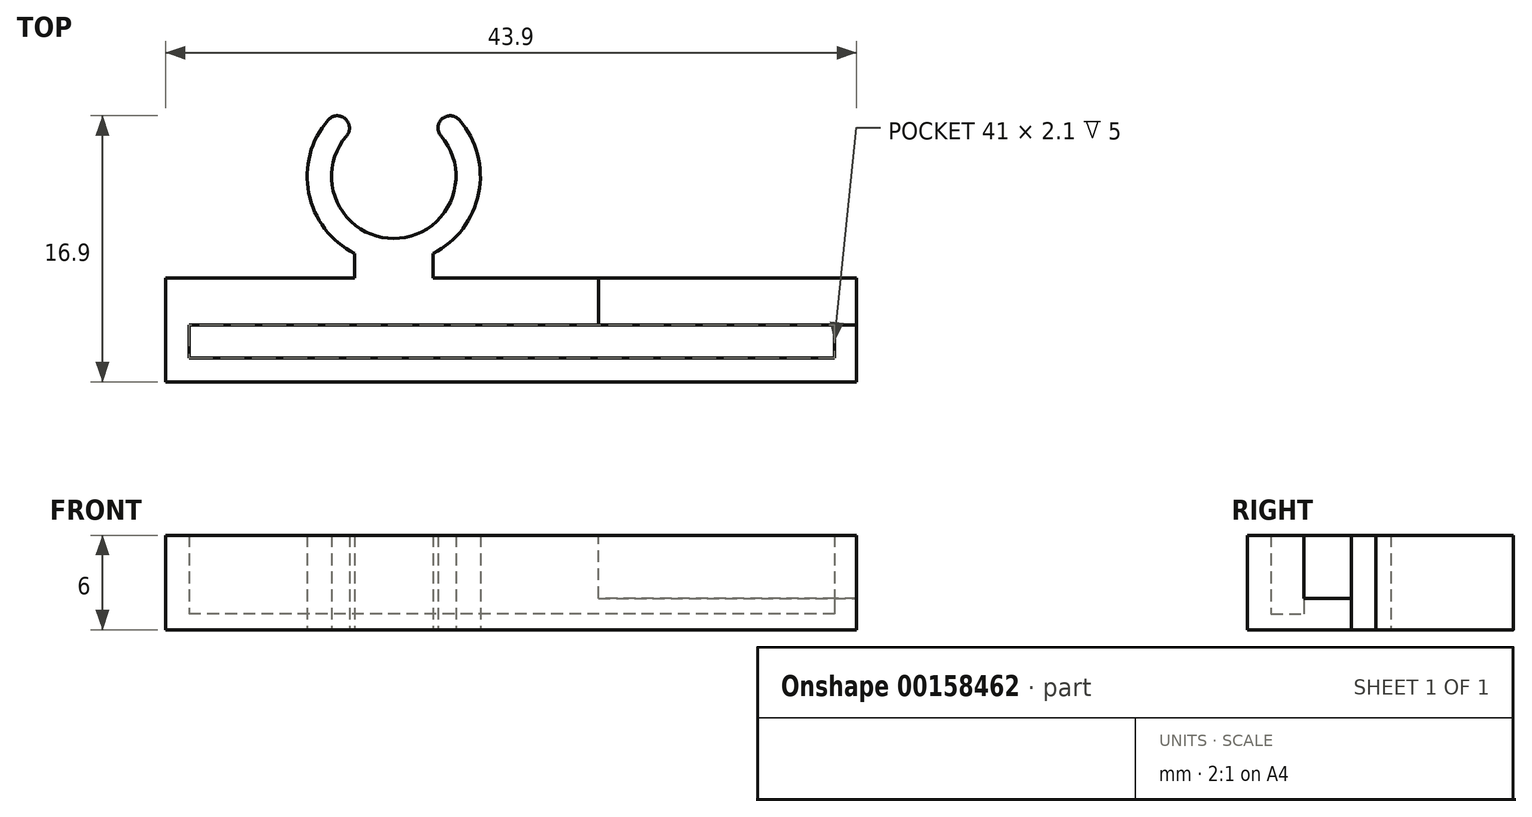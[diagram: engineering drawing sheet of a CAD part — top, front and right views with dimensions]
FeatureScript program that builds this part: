
annotation { "Feature Type Name" : "Feature", "Feature Type Description" : "" }
export const myFeature = defineFeature(function(context is Context, id is Id, definition is map)
    precondition{}
    {
        {
            var Q0;
            Q0=qCreatedBy(makeId("Top.planeOp"),FACE);
            var sketch = newSketch(context, id + "F0", { "sketchPlane" : qUnion([Q0])});
            skArc(sketch, "E0", {"start": v(-3, 2.57) * mm, "mid": v(0, -3.95) * mm, "end": v(3, 2.57) * mm});
            skArc(sketch, "E1", {"start": v(-4.18, 3.58) * mm, "mid": v(-5.4, -1.07) * mm, "end": v(-2.5, -4.9) * mm});
            skLineSegment(sketch, "E2", {"start": v(-3, 2.57) * mm, "end": v(3, 2.57) * mm, "construction": true});
            skLineSegment(sketch, "E3", {"start": v(-3, 2.57) * mm, "end": v(0, 0) * mm, "construction": true});
            skArc(sketch, "E4", {"start": v(-3, 2.57) * mm, "mid": v(-3.08, 3.66) * mm, "end": v(-4.18, 3.58) * mm});
            skLineSegment(sketch, "E5", {"start": v(0, 0) * mm, "end": v(0, 2.57) * mm, "construction": true});
            skArc(sketch, "E6.MirrorCS", {"start": v(3, 2.57) * mm, "mid": v(3.08, 3.66) * mm, "end": v(4.18, 3.58) * mm});
            skLineSegment(sketch, "E7.bottom", {"start": v(-14.5, -6.45) * mm, "end": v(-2.5, -6.45) * mm});
            skLineSegment(sketch, "E7.top", {"start": v(-14.5, -13.05) * mm, "end": v(29.4, -13.05) * mm});
            skLineSegment(sketch, "E7.left", {"start": v(-14.5, -6.45) * mm, "end": v(-14.5, -13.05) * mm});
            skLineSegment(sketch, "E7.right", {"start": v(29.4, -6.45) * mm, "end": v(29.4, -13.05) * mm});
            skLineSegment(sketch, "E8", {"start": v(-2.5, -4.9) * mm, "end": v(-2.5, -6.45) * mm});
            skLineSegment(sketch, "E9", {"start": v(2.5, -4.9) * mm, "end": v(2.5, -6.45) * mm});
            skLineSegment(sketch, "E10.bottom", {"start": v(-13, -9.45) * mm, "end": v(28, -9.45) * mm});
            skLineSegment(sketch, "E10.top", {"start": v(-13, -11.55) * mm, "end": v(28, -11.55) * mm});
            skLineSegment(sketch, "E10.left", {"start": v(-13, -9.45) * mm, "end": v(-13, -11.55) * mm});
            skLineSegment(sketch, "E10.right", {"start": v(28, -9.45) * mm, "end": v(28, -11.55) * mm});
            skLineSegment(sketch, "E11.trimOffspring", {"start": v(2.5, -6.45) * mm, "end": v(29.4, -6.45) * mm});
            skArc(sketch, "E12.trimOffspring", {"start": v(2.5, -4.9) * mm, "mid": v(5.4, -1.07) * mm, "end": v(4.18, 3.58) * mm});
            skSolve(sketch);
        }
        {
            var Q0;
            Q0 = qSketchRegion(id + "F0", true);
            extrude(context, id + "F1", {"entities" : qUnion([Q0]), "depth" : 6 * mm});
        }
        {
            var Q0;
            Q0=makeQuery(id+"F1.opExtrude","CAP_FACE",FACE,{"disambiguationData":[OSD([sQuery(id+"F0.wireOp",EDGE,"E0"),sQuery(id+"F0.wireOp",EDGE,"E1"),sQuery(id+"F0.wireOp",EDGE,"E4"),sQuery(id+"F0.wireOp",EDGE,"E6.MirrorCS"),sQuery(id+"F0.wireOp",EDGE,"E7.bottom"),sQuery(id+"F0.wireOp",EDGE,"E7.top"),sQuery(id+"F0.wireOp",EDGE,"E7.left"),sQuery(id+"F0.wireOp",EDGE,"E7.right"),sQuery(id+"F0.wireOp",EDGE,"E8"),sQuery(id+"F0.wireOp",EDGE,"E9"),sQuery(id+"F0.wireOp",EDGE,"E10.bottom"),sQuery(id+"F0.wireOp",EDGE,"E10.top"),sQuery(id+"F0.wireOp",EDGE,"E10.left"),sQuery(id+"F0.wireOp",EDGE,"E10.right"),sQuery(id+"F0.wireOp",EDGE,"E11.trimOffspring"),sQuery(id+"F0.wireOp",EDGE,"E12.trimOffspring")])],"isStart":false});
            var sketch = newSketch(context, id + "F2", { "sketchPlane" : qUnion([Q0])});
            skLineSegment(sketch, "E13.bottom", {"start": v(29.4, -6.45) * mm, "end": v(13, -6.45) * mm});
            skLineSegment(sketch, "E13.top", {"start": v(29.4, -9.45) * mm, "end": v(13, -9.45) * mm});
            skLineSegment(sketch, "E13.left", {"start": v(29.4, -6.45) * mm, "end": v(29.4, -9.45) * mm});
            skLineSegment(sketch, "E13.right", {"start": v(13, -6.45) * mm, "end": v(13, -9.45) * mm});
            skSolve(sketch);
        }
        {
            var Q0;
            Q0 = qSketchRegion(id + "F2", true);
            extrude(context, id + "F3", {"entities" : qUnion([Q0]), "operationType" : NewBodyOperationType.REMOVE, "oppositeDirection" : true, "depth" : 4 * mm});
        }
        {
            var Q0;
            Q0=makeQuery(id+"F1.opExtrude","CAP_FACE",FACE,{"disambiguationData":[OSD([sQuery(id+"F0.wireOp",EDGE,"E0"),sQuery(id+"F0.wireOp",EDGE,"E1"),sQuery(id+"F0.wireOp",EDGE,"E4"),sQuery(id+"F0.wireOp",EDGE,"E6.MirrorCS"),sQuery(id+"F0.wireOp",EDGE,"E7.bottom"),sQuery(id+"F0.wireOp",EDGE,"E7.top"),sQuery(id+"F0.wireOp",EDGE,"E7.left"),sQuery(id+"F0.wireOp",EDGE,"E7.right"),sQuery(id+"F0.wireOp",EDGE,"E8"),sQuery(id+"F0.wireOp",EDGE,"E9"),sQuery(id+"F0.wireOp",EDGE,"E10.bottom"),sQuery(id+"F0.wireOp",EDGE,"E10.top"),sQuery(id+"F0.wireOp",EDGE,"E10.left"),sQuery(id+"F0.wireOp",EDGE,"E10.right"),sQuery(id+"F0.wireOp",EDGE,"E11.trimOffspring"),sQuery(id+"F0.wireOp",EDGE,"E12.trimOffspring")])],"isStart":true});
            var sketch = newSketch(context, id + "F4", { "sketchPlane" : qUnion([Q0])});
            skLineSegment(sketch, "E14.bottom", {"start": v(-14.5, 13.05) * mm, "end": v(29.4, 13.05) * mm});
            skLineSegment(sketch, "E14.top", {"start": v(-14.5, 6.45) * mm, "end": v(29.4, 6.45) * mm});
            skLineSegment(sketch, "E14.left", {"start": v(-14.5, 13.05) * mm, "end": v(-14.5, 6.45) * mm});
            skLineSegment(sketch, "E14.right", {"start": v(29.4, 13.05) * mm, "end": v(29.4, 6.45) * mm});
            skSolve(sketch);
        }
        {
            var Q0;
            Q0 = qSketchRegion(id + "F4", true);
            extrude(context, id + "F5", {"entities" : qUnion([Q0]), "operationType" : NewBodyOperationType.ADD, "oppositeDirection" : true, "depth" : 1 * mm});
        }
    });
